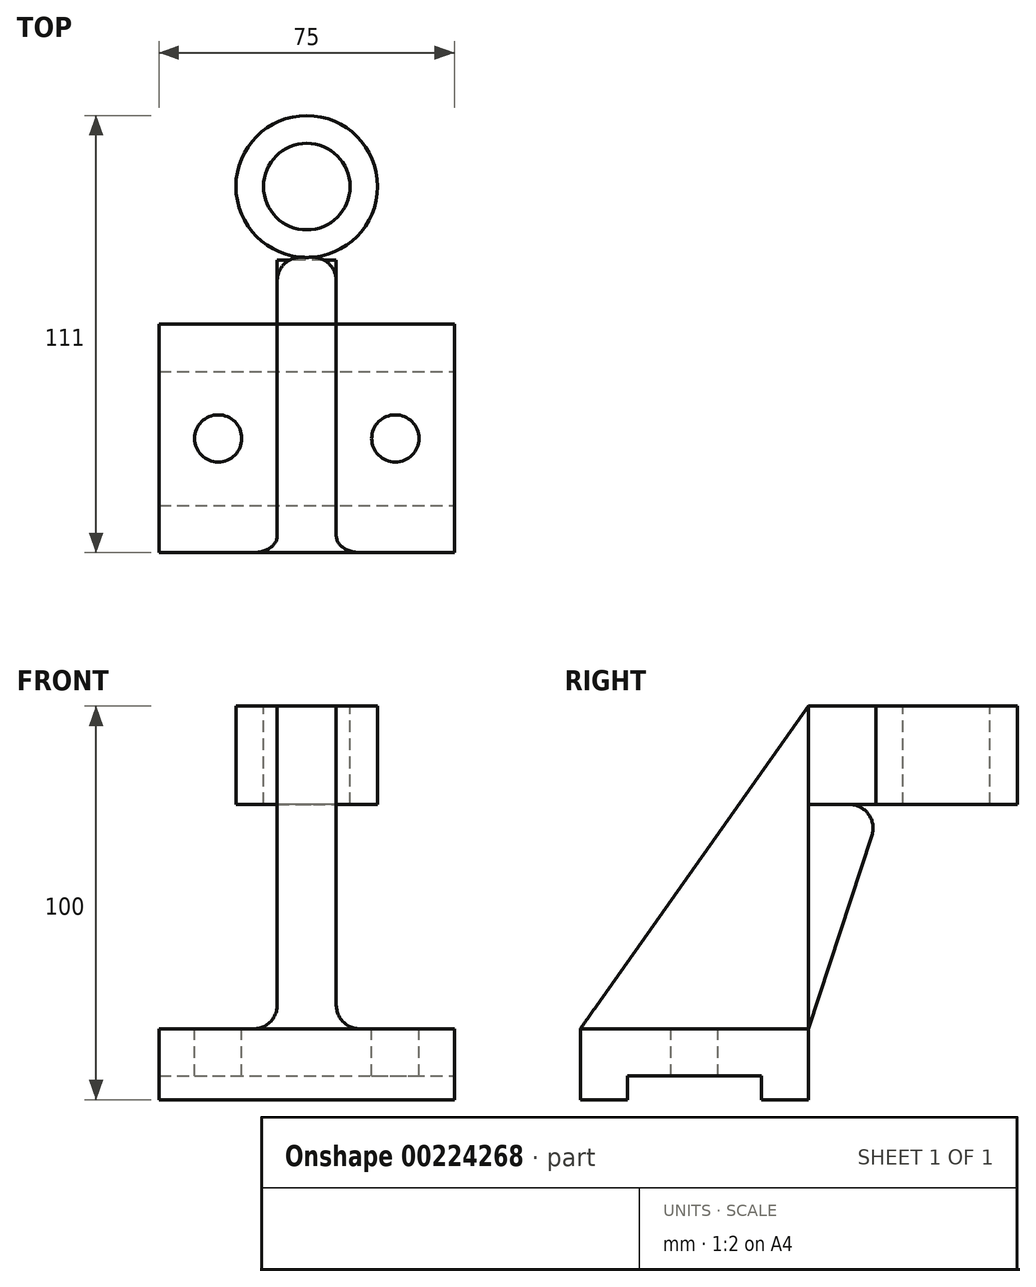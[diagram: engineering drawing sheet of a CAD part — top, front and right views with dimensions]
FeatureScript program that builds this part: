
annotation { "Feature Type Name" : "Feature", "Feature Type Description" : "" }
export const myFeature = defineFeature(function(context is Context, id is Id, definition is map)
    precondition{}
    {
        {
            var Q0;
            Q0=qCreatedBy(makeId("Front.planeOp"),FACE);
            var sketch = newSketch(context, id + "F0", { "sketchPlane" : qUnion([Q0])});
            skLineSegment(sketch, "E0.bottom", {"start": v(37.5, 9) * mm, "end": v(7.5, 9) * mm});
            skLineSegment(sketch, "E0.top", {"start": v(37.5, -9) * mm, "end": v(-37.5, -9) * mm});
            skLineSegment(sketch, "E0.left", {"start": v(37.5, 9) * mm, "end": v(37.5, -9) * mm});
            skLineSegment(sketch, "E0.right", {"start": v(-37.5, 9) * mm, "end": v(-37.5, -9) * mm});
            skPoint(sketch, "E0.middle", {"position": v(0, 0) * mm});
            skLineSegment(sketch, "E1", {"start": v(-7.5, 9) * mm, "end": v(-7.5, 91) * mm});
            skLineSegment(sketch, "E2", {"start": v(-7.5, 91) * mm, "end": v(7.5, 91) * mm});
            skLineSegment(sketch, "E3", {"start": v(7.5, 91) * mm, "end": v(7.5, 9) * mm});
            skLineSegment(sketch, "E4.trimOffspring", {"start": v(-7.5, 9) * mm, "end": v(-37.5, 9) * mm});
            skSolve(sketch);
        }
        {
            var Q0;
            Q0=makeQuery(id+"F0.imprint","IMPRINT",FACE,{"disambiguationData":[TD([[makeQuery(id+"F0.imprint","IMPRINT",EDGE,{"derivedFrom":sQuery(id+"F0.wireOp",EDGE,"E0.bottom")}),1.0]])]});
            extrude(context, id + "F1", {"entities" : qUnion([Q0]), "endBound" : BoundingType.SYMMETRIC, "depth" : 58 * mm});
        }
        {
            var Q0;
            Q0=makeQuery(id+"F1.opExtrude","SWEPT_FACE",FACE,{"disambiguationData":[OSD([sQuery(id+"F0.wireOp",EDGE,"E0.left")])]});
            var sketch = newSketch(context, id + "F2", { "sketchPlane" : qUnion([Q0])});
            skLineSegment(sketch, "E5", {"start": v(-17, -9) * mm, "end": v(-17, -3) * mm});
            skLineSegment(sketch, "E6", {"start": v(-17, -3) * mm, "end": v(17, -3) * mm});
            skLineSegment(sketch, "E7", {"start": v(17, -3) * mm, "end": v(17, -9) * mm});
            skLineSegment(sketch, "E8", {"start": v(17, -9) * mm, "end": v(-17, -9) * mm});
            skSolve(sketch);
        }
        {
            var Q0;
            Q0=makeQuery(id+"F2.imprint","IMPRINT",FACE,{"disambiguationData":[TD([[makeQuery(id+"F2.imprint","IMPRINT",EDGE,{"derivedFrom":sQuery(id+"F2.wireOp",EDGE,"E5")}),-1.0]])]});
            extrude(context, id + "F3", {"entities" : qUnion([Q0]), "operationType" : NewBodyOperationType.REMOVE, "endBound" : BoundingType.THROUGH_ALL, "oppositeDirection" : true, "depth" : 25 * mm});
        }
        {
            var Q0;
            Q0=makeQuery(id+"F1.opExtrude","SWEPT_FACE",FACE,{"disambiguationData":[OSD([sQuery(id+"F0.wireOp",EDGE,"E2")])]});
            cPlane(context, id + "F4", {"entities" : qUnion([Q0]), "cplaneType" : CPlaneType.OFFSET, "offset" : 0 * mm, "width" : 150 * mm, "height" : 150 * mm});
        }
        {
            var Q0;
            Q0=qCreatedBy(id+"F4.planeOp",FACE);
            var sketch = newSketch(context, id + "F5", { "sketchPlane" : qUnion([Q0])});
            skCircle(sketch, "E9", {"center": v(0, 64) * mm, "radius": 18 * mm});
            skCircle(sketch, "E10", {"center": v(0, 64) * mm, "radius": 11 * mm});
            skLineSegment(sketch, "E11", {"start": v(-7.5, 29) * mm, "end": v(7.5, 29) * mm});
            skLineSegment(sketch, "E12", {"start": v(-7.5, 29) * mm, "end": v(-7.5, 47.64) * mm});
            skLineSegment(sketch, "E13", {"start": v(7.5, 29) * mm, "end": v(7.5, 47.64) * mm});
            skSolve(sketch);
        }
        {
            var Q0;
            Q0=makeQuery(id+"F5.imprint","IMPRINT",FACE,{"disambiguationData":[TD([[makeQuery(id+"F5.imprint","IMPRINT",EDGE,{"derivedFrom":sQuery(id+"F5.wireOp",EDGE,"E11")}),1.0]])]});
            extrude(context, id + "F6", {"entities" : qUnion([Q0]), "oppositeDirection" : true, "depth" : 25 * mm});
        }
        {
            var Q0;
            Q0=makeQuery(id+"F1.opExtrude","SWEPT_FACE",FACE,{"disambiguationData":[OSD([sQuery(id+"F0.wireOp",EDGE,"E3")])]});
            var sketch = newSketch(context, id + "F7", { "sketchPlane" : qUnion([Q0])});
            skLineSegment(sketch, "E14", {"start": v(29, 91) * mm, "end": v(-29, 9) * mm});
            skLineSegment(sketch, "E15.0", {"start": v(-29, 91) * mm, "end": v(29, 91) * mm});
            skLineSegment(sketch, "E16.0", {"start": v(-29, 91) * mm, "end": v(-29, 9) * mm});
            skSolve(sketch);
        }
        {
            var Q0;
            Q0=makeQuery(id+"F7.imprint","IMPRINT",FACE,{"disambiguationData":[TD([[makeQuery(id+"F7.imprint","IMPRINT",EDGE,{"derivedFrom":sQuery(id+"F7.wireOp",EDGE,"E14")}),-1.0]])]});
            extrude(context, id + "F8", {"entities" : qUnion([Q0]), "operationType" : NewBodyOperationType.REMOVE, "oppositeDirection" : true, "depth" : 25 * mm});
        }
        {
            var Q0;
            Q0=makeQuery(id+"F5.imprint","IMPRINT",FACE,{"disambiguationData":[TD([[makeQuery(id+"F5.imprint","IMPRINT",EDGE,{"derivedFrom":sQuery(id+"F5.wireOp",EDGE,"E10")}),-1.0]])]});
            extrude(context, id + "F9", {"entities" : qUnion([Q0]), "oppositeDirection" : true, "depth" : 25 * mm});
        }
        {
            var Q0;
            Q0=makeQuery(id+"F1.opExtrude","SWEPT_FACE",FACE,{"disambiguationData":[OSD([sQuery(id+"F0.wireOp",EDGE,"E3")])]});
            var sketch = newSketch(context, id + "F10", { "sketchPlane" : qUnion([Q0])});
            skLineSegment(sketch, "E17", {"start": v(29, 9) * mm, "end": v(47.64, 66) * mm});
            skLineSegment(sketch, "E18.0", {"start": v(29, 66) * mm, "end": v(47.64, 66) * mm});
            skLineSegment(sketch, "E19.0", {"start": v(29, 91) * mm, "end": v(29, 9) * mm});
            skSolve(sketch);
        }
        {
            var Q0;
            Q0 = qSketchRegion(id + "F10", true);
            extrude(context, id + "F11", {"entities" : qUnion([Q0]), "oppositeDirection" : true, "depth" : 15 * mm});
        }
        {
            var Q0;
            Q0=makeQuery(id+"F1.opExtrude","SWEPT_EDGE",EDGE,{"disambiguationData":[OSD([sQuery(id+"F0.wireOp",EDGE,"E0.bottom"),sQuery(id+"F0.wireOp",EDGE,"E3")])]});
            var Q1;
            Q1=makeQuery(id+"F1.opExtrude","SWEPT_EDGE",EDGE,{"disambiguationData":[OSD([sQuery(id+"F0.wireOp",EDGE,"E1"),sQuery(id+"F0.wireOp",EDGE,"E4.trimOffspring")])]});
            var Q2;
            Q2=makeQuery(id+"F11.opExtrude","SWEPT_EDGE",EDGE,{"disambiguationData":[OSD([sQuery(id+"F10.wireOp",EDGE,"E17"),sQuery(id+"F10.wireOp",EDGE,"E18.0")])]});
            var Q3;
            Q3=makeQuery(id+"F6.opExtrude","SWEPT_EDGE",EDGE,{"disambiguationData":[OSD([sQuery(id+"F5.wireOp",EDGE,"E9"),sQuery(id+"F5.wireOp",EDGE,"E13")])]});
            var Q4;
            Q4=makeQuery(id+"F6.opExtrude","SWEPT_EDGE",EDGE,{"disambiguationData":[OSD([sQuery(id+"F5.wireOp",EDGE,"E9"),sQuery(id+"F5.wireOp",EDGE,"E12")])]});
            fillet(context, id + "F12", {"entities" : qUnion([Q0, Q1, Q2, Q3, Q4]), "radius" : 6 * mm, "tangentPropagation" : true, "allowEdgeOverflow" : false});
        }
        {
            var Q0;
            Q0=makeQuery(id+"F1.opExtrude","SWEPT_FACE",FACE,{"disambiguationData":[OSD([sQuery(id+"F0.wireOp",EDGE,"E0.bottom")])]});
            var sketch = newSketch(context, id + "F13", { "sketchPlane" : qUnion([Q0])});
            skCircle(sketch, "E20", {"center": v(22.5, 0) * mm, "radius": 6 * mm});
            skCircle(sketch, "E21", {"center": v(-22.5, 0) * mm, "radius": 6 * mm});
            skSolve(sketch);
        }
        {
            var Q0;
            Q0=makeQuery(id+"F13.imprint","IMPRINT",FACE,{"disambiguationData":[TD([[makeQuery(id+"F13.imprint","IMPRINT",EDGE,{"derivedFrom":sQuery(id+"F13.wireOp",EDGE,"E21")}),1.0]])]});
            var Q1;
            Q1=makeQuery(id+"F13.imprint","IMPRINT",FACE,{"disambiguationData":[TD([[makeQuery(id+"F13.imprint","IMPRINT",EDGE,{"derivedFrom":sQuery(id+"F13.wireOp",EDGE,"E20")}),1.0]])]});
            extrude(context, id + "F14", {"entities" : qUnion([Q0, Q1]), "operationType" : NewBodyOperationType.REMOVE, "oppositeDirection" : true, "depth" : 25 * mm});
        }
    });
